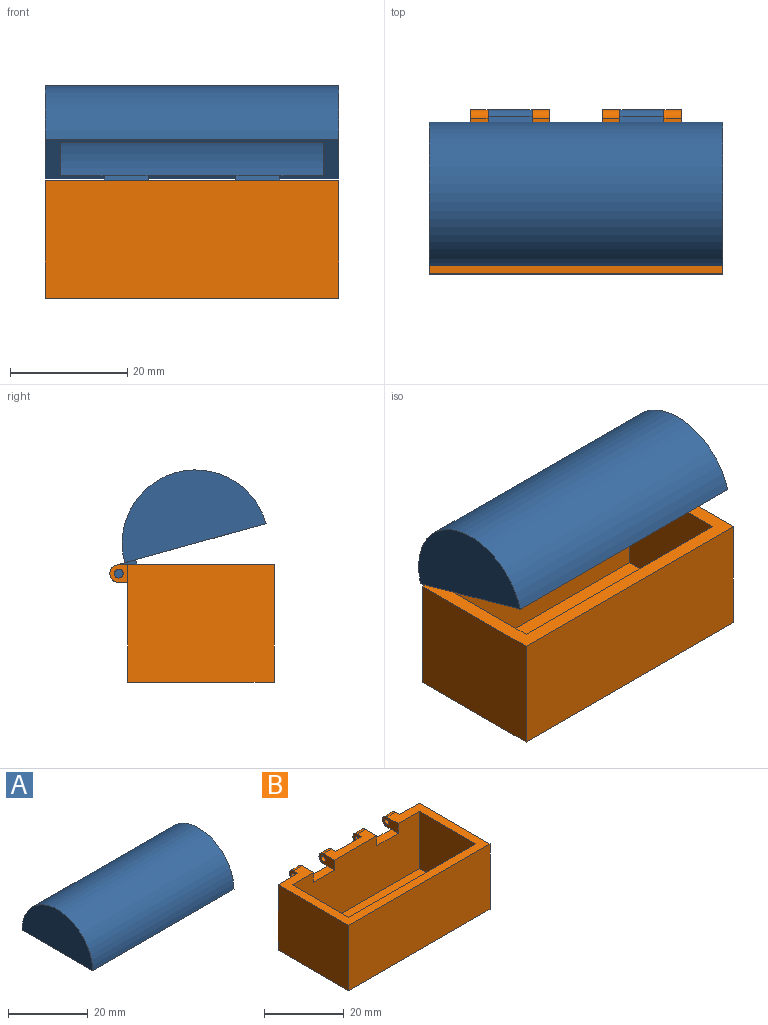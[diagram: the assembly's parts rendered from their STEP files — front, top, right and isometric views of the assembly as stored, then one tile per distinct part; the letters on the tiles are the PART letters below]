
ASSEMBLY  parts=2 mates=1
PART A: 28 faces, bbox 50x28x15.5 mm
  f0: plane 4.92x3mm, normal (-1,0,0), area 12mm2, adj f2,f7,f9,f16,f19,f22
  f1: plane 4.92x3mm, normal (1,0,0), area 12mm2, adj f2,f7,f8,f16,f19,f20
  f2: plane 7.5x3.42mm, normal (0,0,-1), area 25.7mm2, adj f0,f1,f16,f19
  f3: plane 4.92x3mm, normal (1,0,0), area 12mm2, adj f5,f6,f9,f17,f18,f26
  f4: plane 4.92x3mm, normal (-1,0,0), area 12mm2, adj f5,f6,f8,f17,f18,f24
  f5: plane 7.5x3.42mm, normal (0,0,-1), area 25.7mm2, adj f3,f4,f17,f18
  f6: plane 7.5x1.5mm, normal (0,0,1), area 11.2mm2, adj f3,f4,f10,f18
  f7: plane 7.5x1.5mm, normal (0,0,1), area 11.2mm2, adj f0,f1,f10,f19
  f8: plane 50x25mm, normal (0,0,-1), area 240.4mm2, adj f1,f4,f10,f11,f12,f13,f14,f15
  f9: plane 15x1.92mm, normal (0,0,-1), area 28.9mm2, adj f0,f3,f10,f13
  f10: cylinder r=12.5mm len=50mm, axis (1,0,0), area 1963.5mm2, adj f6,f7,f8,f9,f11,f12
  f11: plane 25x12.5mm, normal (-1,0,0), area 245.4mm2, adj f8,f10
  f12: plane 25x12.5mm, normal (1,0,0), area 245.4mm2, adj f8,f10
  f13: cylinder r=10.58mm len=45mm, axis (1,0,0), area 1495.1mm2, adj f8,f9,f14,f15,f16,f17
  f14: plane 21.15x10.58mm, normal (1,0,0), area 175.7mm2, adj f8,f13
  f15: plane 21.15x10.58mm, normal (-1,0,0), area 175.7mm2, adj f8,f13
  f16: plane 7.5x3mm, normal (0,-1,0), area 22.5mm2, adj f0,f1,f2,f13
  f17: plane 7.5x3mm, normal (0,-1,0), area 22.5mm2, adj f3,f4,f5,f13
  f18: cylinder r=1.5mm len=7.5mm, axis (1,0,0), area 35.3mm2, adj f3,f4,f5,f6
  f19: cylinder r=1.5mm len=7.5mm, axis (1,0,0), area 35.3mm2, adj f0,f1,f2,f7
  f20: cylinder r=0.75mm len=3mm, axis (-1,0,0), area 14.1mm2, adj f1,f21
  f21: plane 1.5x1.5mm, normal (1,0,0), area 1.8mm2, adj f20
  f22: cylinder r=0.75mm len=3mm, axis (1,0,0), area 14.1mm2, adj f0,f23
  f23: plane 1.5x1.5mm, normal (-1,0,0), area 1.8mm2, adj f22
  f24: cylinder r=0.75mm len=3mm, axis (1,0,0), area 14.1mm2, adj f4,f25
  f25: plane 1.5x1.5mm, normal (-1,0,0), area 1.8mm2, adj f24
  f26: cylinder r=0.75mm len=3mm, axis (-1,0,0), area 14.1mm2, adj f3,f27
  f27: plane 1.5x1.5mm, normal (1,0,0), area 1.8mm2, adj f26
PART B: 243 faces, bbox 50x28x20 mm
  f0: plane 50x25mm, normal (0,0,-1), area 1214.1mm2, adj f12,f13,f14,f15,f34,f35,f36,f37
  f1: plane 5.5x3mm, normal (1,0,0), area 13.8mm2, adj f5,f17,f22,f25,f30,f31
  f2: plane 5.5x3mm, normal (-1,0,0), area 13.8mm2, adj f4,f17,f22,f23,f32,f33
  f3: plane 3x3mm, normal (-1,0,0), area 6.3mm2, adj f5,f12,f25,f30,f31
  f4: plane 50x26.5mm, normal (0,0,1), area 284mm2, adj f2,f7,f10,f12,f13,f14,f15,f16
  f5: plane 15x4mm, normal (0,0,1), area 46.5mm2, adj f1,f3,f6,f8,f12,f17,f28,f31
  f6: plane 5.5x3mm, normal (-1,0,0), area 13.8mm2, adj f5,f9,f17,f21,f27,f28
  f7: plane 5.5x3mm, normal (1,0,0), area 13.8mm2, adj f4,f11,f17,f21,f26,f29
  f8: plane 3x3mm, normal (1,0,0), area 6.3mm2, adj f5,f9,f12,f27,f28
  f9: plane 3x1.5mm, normal (0,0,-1), area 4.5mm2, adj f6,f8,f12,f28
  f10: plane 3x3mm, normal (-1,0,0), area 6.3mm2, adj f4,f11,f12,f26,f29
  f11: plane 3x1.5mm, normal (0,0,-1), area 4.5mm2, adj f7,f10,f12,f29
  f12: plane 50x20mm, normal (0,1,0), area 919mm2, adj f0,f3,f4,f5,f8,f9,f10,f11
  f13: plane 25x20mm, normal (1,0,0), area 500mm2, adj f0,f4,f12,f15
  f14: plane 25x20mm, normal (-1,0,0), area 500mm2, adj f0,f4,f12,f15
  f15: plane 50x20mm, normal (0,-1,0), area 1000mm2, adj f0,f4,f13,f14
  f16: plane 20x17.5mm, normal (-1,0,0), area 350mm2, adj f4,f17,f19,f20
  f17: plane 45x17.5mm, normal (0,-1,0), area 742.5mm2, adj f1,f2,f4,f5,f6,f7,f16,f18
  f18: plane 20x17.5mm, normal (1,0,0), area 350mm2, adj f4,f17,f19,f20
  f19: plane 45x17.5mm, normal (0,1,0), area 787.5mm2, adj f4,f16,f18,f20
  f20: plane 45x20mm, normal (0,0,1), area 900mm2, adj f16,f17,f18,f19
  f21: plane 7.5x2.5mm, normal (0,0,1), area 18.8mm2, adj f6,f7,f12,f17
  f22: plane 7.5x2.5mm, normal (0,0,1), area 18.8mm2, adj f1,f2,f12,f17
  f23: plane 3x1.5mm, normal (0,0,-1), area 4.5mm2, adj f2,f12,f24,f33
  f24: plane 3x3mm, normal (1,0,0), area 6.3mm2, adj f4,f12,f23,f32,f33
  f25: plane 3x1.5mm, normal (0,0,-1), area 4.5mm2, adj f1,f3,f12,f31
  f26: cylinder r=0.75mm len=3mm, axis (-1,0,0), area 14.1mm2, adj f7,f10
  f27: cylinder r=0.75mm len=3mm, axis (-1,0,0), area 14.1mm2, adj f6,f8
  f28: cylinder r=1.5mm len=3mm, axis (-1,0,0), area 14.1mm2, adj f5,f6,f8,f9
  f29: cylinder r=1.5mm len=3mm, axis (-1,0,0), area 14.1mm2, adj f4,f7,f10,f11
  f30: cylinder r=0.75mm len=3mm, axis (1,0,0), area 14.1mm2, adj f1,f3
  f31: cylinder r=1.5mm len=3mm, axis (1,0,0), area 14.1mm2, adj f1,f3,f5,f25
  f32: cylinder r=0.75mm len=3mm, axis (1,0,0), area 14.1mm2, adj f2,f24
  f33: cylinder r=1.5mm len=3mm, axis (1,0,0), area 14.1mm2, adj f2,f4,f23,f24
  f34: plane 1x0.27mm, normal (-0.53,-0.85,0), area 0.3mm2, adj f0,f35,f37,f38
  f35: extruded ~1x0.63mm, area 0.7mm2, adj f0,f34,f36,f38
  f36: plane 1x0.26mm, normal (0.49,0.87,0), area 0.3mm2, adj f0,f35,f37,f38
  f37: extruded ~1x0.65mm, area 0.7mm2, adj f0,f34,f36,f38
  f38: plane 0.8x0.61mm, normal (0,0,-1), area 0.2mm2, adj f34,f35,f36,f37
  f39: plane 1x0.95mm, normal (-1,0,0), area 1mm2, adj f40,f58,f59,f240
  f40: plane 1.26x1mm, normal (0,-1,0), area 1.3mm2, adj f39,f41,f59,f240
  f41: plane 1x0.95mm, normal (1,0,0), area 1mm2, adj f40,f58,f59,f240
  f42: plane 1.26x1mm, normal (0,-1,0), area 1.3mm2, adj f43,f55,f59,f61
  f43: plane 1x0.91mm, normal (1,0,0), area 0.9mm2, adj f42,f44,f59,f61
  f44: plane 1.26x1mm, normal (0,1,0), area 1.3mm2, adj f43,f55,f59,f61
  f45: plane 1x0.93mm, normal (1,0,0), area 0.9mm2, adj f46,f56,f59,f60
  f46: plane 1.26x1mm, normal (0,1,0), area 1.3mm2, adj f45,f47,f59,f60
  f47: plane 1x0.93mm, normal (-1,0,0), area 0.9mm2, adj f46,f56,f59,f60
  f48: plane 1x0.33mm, normal (0,1,0), area 0.3mm2, adj f0,f49,f57,f59
  f49: plane 3.78x1mm, normal (-1,0,0), area 3.8mm2, adj f0,f48,f50,f59
  f50: plane 1.94x1mm, normal (0,1,0), area 1.9mm2, adj f0,f49,f51,f59
  f51: plane 3.78x1mm, normal (1,0,0), area 3.8mm2, adj f0,f50,f52,f59
  f52: plane 1x0.43mm, normal (0,1,0), area 0.4mm2, adj f0,f51,f53,f59
  f53: plane 1x0.33mm, normal (1,0,0), area 0.3mm2, adj f0,f52,f54,f59
  f54: plane 2.7x1mm, normal (0,-1,0), area 2.7mm2, adj f0,f53,f57,f59
  f55: plane 1x0.91mm, normal (-1,0,0), area 0.9mm2, adj f42,f44,f59,f61
  f56: plane 1.26x1mm, normal (0,-1,0), area 1.3mm2, adj f45,f47,f59,f60
  f57: plane 1x0.33mm, normal (-1,0,0), area 0.3mm2, adj f0,f48,f54,f59
  f58: plane 1.26x1mm, normal (0,1,0), area 1.3mm2, adj f39,f41,f59,f240
  f59: plane 4.11x2.7mm, normal (0,0,-1), area 4.7mm2, adj f39,f40,f41,f42,f43,f44,f45,f46
  f60: plane 1.26x0.93mm, normal (0,0,-1), area 1.2mm2, adj f45,f46,f47,f56
  f61: plane 1.26x0.91mm, normal (0,0,-1), area 1.1mm2, adj f42,f43,f44,f55
  f62: plane 2.12x1mm, normal (0,1,0), area 2.1mm2, adj f0,f63,f81,f82
  f63: plane 1x0.35mm, normal (1,0,0), area 0.3mm2, adj f0,f62,f64,f82
  f64: plane 1x0.61mm, normal (0,-1,0), area 0.6mm2, adj f0,f63,f65,f82
  f65: plane 1.44x1mm, normal (1,0,0), area 1.4mm2, adj f0,f64,f66,f82
  f66: plane 1x0.66mm, normal (0,1,0), area 0.7mm2, adj f0,f65,f67,f82
  f67: plane 1x0.34mm, normal (1,0,0), area 0.3mm2, adj f0,f66,f68,f82
  f68: plane 1x0.66mm, normal (0,-1,0), area 0.7mm2, adj f0,f67,f69,f82
  f69: plane 2.06x1mm, normal (1,0,0), area 2.1mm2, adj f0,f68,f70,f82
  f70: plane 1x0.34mm, normal (0,-1,0), area 0.3mm2, adj f0,f69,f71,f82
  f71: plane 2.06x1mm, normal (-1,0,0), area 2.1mm2, adj f0,f70,f72,f82
  f72: plane 1x0.64mm, normal (0,-1,0), area 0.6mm2, adj f0,f71,f73,f82
  f73: plane 1x0.34mm, normal (-1,0,0), area 0.3mm2, adj f0,f72,f74,f82
  f74: plane 1x0.64mm, normal (0,1,0), area 0.6mm2, adj f0,f73,f75,f82
  f75: plane 1.44x1mm, normal (-1,0,0), area 1.4mm2, adj f0,f74,f76,f82
  f76: plane 1x0.81mm, normal (0,-1,0), area 0.8mm2, adj f0,f75,f77,f82
  f77: extruded ~3.74x1mm, area 3.9mm2, adj f0,f76,f78,f82
  f78: extruded ~1x0.77mm, area 1mm2, adj f0,f77,f79,f82
  f79: extruded ~1x0.26mm, area 0.3mm2, adj f0,f78,f80,f82
  f80: extruded ~1x0.65mm, area 0.7mm2, adj f0,f79,f81,f82
  f81: extruded ~3.73x1mm, area 3.8mm2, adj f0,f62,f80,f82
  f82: plane 4.18x2.7mm, normal (0,0,-1), area 4mm2, adj f62,f63,f64,f65,f66,f67,f68,f69
  f83: plane 1x0.29mm, normal (1,0,0), area 0.3mm2, adj f0,f84,f86,f87
  f84: plane 1.38x1mm, normal (0,-1,0), area 1.4mm2, adj f0,f83,f85,f87
  f85: plane 1x0.29mm, normal (-1,0,0), area 0.3mm2, adj f0,f84,f86,f87
  f86: plane 1.38x1mm, normal (0,1,0), area 1.4mm2, adj f0,f83,f85,f87
  f87: plane 1.38x0.29mm, normal (0,0,-1), area 0.4mm2, adj f83,f84,f85,f86
  f88: plane 1.37x1mm, normal (0,-1,0), area 1.4mm2, adj f0,f89,f91,f92
  f89: plane 1x0.29mm, normal (-1,0,0), area 0.3mm2, adj f0,f88,f90,f92
  f90: plane 1.37x1mm, normal (0,1,0), area 1.4mm2, adj f0,f89,f91,f92
  f91: plane 1x0.29mm, normal (1,0,0), area 0.3mm2, adj f0,f88,f90,f92
  f92: plane 1.37x0.29mm, normal (0,0,-1), area 0.4mm2, adj f88,f89,f90,f91
  f93: plane 1x0.3mm, normal (-1,0,0), area 0.3mm2, adj f0,f94,f96,f97
  f94: plane 1.75x1mm, normal (0,1,0), area 1.8mm2, adj f0,f93,f95,f97
  f95: plane 1x0.3mm, normal (1,0,0), area 0.3mm2, adj f0,f94,f96,f97
  f96: plane 1.75x1mm, normal (0,-1,0), area 1.8mm2, adj f0,f93,f95,f97
  f97: plane 1.75x0.3mm, normal (0,0,-1), area 0.5mm2, adj f93,f94,f95,f96
  f98: plane 3.48x1mm, normal (0,1,0), area 3.5mm2, adj f0,f99,f101,f102
  f99: plane 1x0.39mm, normal (1,0,0), area 0.4mm2, adj f0,f98,f100,f102
  f100: plane 3.48x1mm, normal (0,-1,0), area 3.5mm2, adj f0,f99,f101,f102
  f101: plane 1x0.39mm, normal (-1,0,0), area 0.4mm2, adj f0,f98,f100,f102
  f102: plane 3.48x0.39mm, normal (0,0,-1), area 1.3mm2, adj f98,f99,f100,f101
  f103: plane 4.3x1mm, normal (0,1,0), area 4.3mm2, adj f0,f104,f106,f107
  f104: plane 1x0.4mm, normal (1,0,0), area 0.4mm2, adj f0,f103,f105,f107
  f105: plane 4.3x1mm, normal (0,-1,0), area 4.3mm2, adj f0,f104,f106,f107
  f106: plane 1x0.4mm, normal (-1,0,0), area 0.4mm2, adj f0,f103,f105,f107
  f107: plane 4.3x0.4mm, normal (0,0,-1), area 1.7mm2, adj f103,f104,f105,f106
  f108: plane 1x0.26mm, normal (1,0,0), area 0.3mm2, adj f0,f109,f119,f120
  f109: plane 2.25x1mm, normal (0,-1,0), area 2.3mm2, adj f0,f108,f110,f120
  f110: plane 1x0.39mm, normal (-1,0,0), area 0.4mm2, adj f0,f109,f111,f120
  f111: plane 1x0.99mm, normal (0,1,0), area 1mm2, adj f0,f110,f112,f120
  f112: extruded ~1x0.59mm, area 0.6mm2, adj f0,f111,f113,f120
  f113: extruded ~2.24x1.4mm, area 2.7mm2, adj f0,f112,f114,f120
  f114: extruded ~1.06x1.04mm, area 1.7mm2, adj f0,f113,f115,f120
  f115: extruded ~1.05x1mm, area 1.2mm2, adj f0,f114,f116,f120
  f116: plane 1x0.26mm, normal (0.7,-0.71,0), area 0.4mm2, adj f0,f115,f117,f120
  f117: extruded ~1x0.74mm, area 0.9mm2, adj f0,f116,f118,f120
  f118: extruded ~1x0.71mm, area 1.1mm2, adj f0,f117,f119,f120
  f119: extruded ~2.31x1.64mm, area 2.9mm2, adj f0,f108,f118,f120
  f120: plane 3.65x2.27mm, normal (0,0,-1), area 2.9mm2, adj f108,f109,f110,f111,f112,f113,f114,f115
  f121: plane 1x0.42mm, normal (0,-1,0), area 0.4mm2, adj f0,f122,f133,f134
  f122: plane 1x0.19mm, normal (0.61,0.8,0), area 0.2mm2, adj f0,f121,f123,f134
  f123: extruded ~1x0.5mm, area 0.7mm2, adj f0,f122,f124,f134
  f124: plane 1x0.24mm, normal (-0.64,-0.77,0), area 0.3mm2, adj f0,f123,f125,f134
  f125: extruded ~1x0.44mm, area 0.6mm2, adj f0,f124,f126,f134
  f126: plane 1x0.92mm, normal (0,-1,0), area 0.9mm2, adj f0,f125,f127,f134
  f127: plane 1x0.29mm, normal (-1,0,0), area 0.3mm2, adj f0,f126,f128,f134
  f128: plane 1.25x1mm, normal (0,1,0), area 1.3mm2, adj f0,f127,f129,f134
  f129: extruded ~1x0.29mm, area 0.3mm2, adj f0,f128,f130,f134
  f130: plane 1x0.32mm, normal (-0.27,0.96,0), area 0.3mm2, adj f0,f129,f131,f134
  f131: extruded ~1.06x1mm, area 1.3mm2, adj f0,f130,f132,f134
  f132: extruded ~1x0.25mm, area 0.3mm2, adj f0,f131,f133,f134
  f133: extruded ~1x0.63mm, area 0.8mm2, adj f0,f121,f132,f134
  f134: plane 2.17x1.31mm, normal (0,0,-1), area 1mm2, adj f121,f122,f123,f124,f125,f126,f127,f128
  f135: plane 1.1x1mm, normal (0,-1,0), area 1.1mm2, adj f136,f168,f169,f241
  f136: plane 1x0.45mm, normal (1,0,0), area 0.5mm2, adj f135,f137,f169,f241
  f137: plane 1.17x1mm, normal (0,1,0), area 1.2mm2, adj f136,f168,f169,f241
  f138: plane 1x0.45mm, normal (-1,0,0), area 0.4mm2, adj f139,f166,f169,f170
  f139: plane 1.28x1mm, normal (0,-1,0), area 1.3mm2, adj f138,f140,f169,f170
  f140: plane 1x0.45mm, normal (1,0,0), area 0.4mm2, adj f139,f166,f169,f170
  f141: plane 1.8x1mm, normal (0,1,0), area 1.8mm2, adj f0,f142,f167,f169
  f142: plane 1x0.45mm, normal (-1,0,0), area 0.5mm2, adj f0,f141,f143,f169
  f143: plane 1.64x1mm, normal (0,-1,0), area 1.6mm2, adj f0,f142,f144,f169
  f144: plane 1.06x1mm, normal (-1,0,0), area 1.1mm2, adj f0,f143,f145,f169
  f145: plane 3.57x1mm, normal (0,1,0), area 3.6mm2, adj f0,f144,f146,f169
  f146: plane 1x0.31mm, normal (1,0,0), area 0.3mm2, adj f0,f145,f147,f169
  f147: plane 1.58x1mm, normal (0,-1,0), area 1.6mm2, adj f0,f146,f148,f169
  f148: plane 1x0.45mm, normal (1,0,0), area 0.4mm2, adj f0,f147,f149,f169
  f149: plane 1.41x1mm, normal (0,1,0), area 1.4mm2, adj f0,f148,f150,f169
  f150: extruded ~1.07x1mm, area 1.1mm2, adj f0,f149,f151,f169
  f151: plane 1.29x1mm, normal (0,-1,0), area 1.3mm2, adj f0,f150,f152,f169
  f152: extruded ~1.59x1mm, area 1.9mm2, adj f0,f151,f153,f169
  f153: extruded ~1x0.29mm, area 0.4mm2, adj f0,f152,f154,f169
  f154: extruded ~1.64x1.13mm, area 2mm2, adj f0,f153,f155,f169
  f155: plane 1.12x1mm, normal (1,0,0), area 1.1mm2, adj f0,f154,f156,f169
  f156: plane 1x0.36mm, normal (0,-1,0), area 0.4mm2, adj f0,f155,f157,f169
  f157: plane 1.26x1mm, normal (-1,0,0), area 1.3mm2, adj f0,f156,f158,f169
  f158: plane 1.41x1mm, normal (0,-1,0), area 1.4mm2, adj f0,f157,f159,f169
  f159: extruded ~1x0.7mm, area 0.7mm2, adj f0,f158,f160,f169
  f160: extruded ~1x0.18mm, area 0.2mm2, adj f0,f159,f161,f169
  f161: extruded ~1x0.55mm, area 0.6mm2, adj f0,f160,f162,f169
  f162: extruded ~1x0.34mm, area 0.4mm2, adj f0,f161,f163,f169
  f163: extruded ~1x0.62mm, area 0.6mm2, adj f0,f162,f164,f169
  f164: extruded ~1x0.3mm, area 0.3mm2, adj f0,f163,f165,f169
  f165: extruded ~1.09x1mm, area 1.1mm2, adj f0,f164,f167,f169
  f166: plane 1.28x1mm, normal (0,1,0), area 1.3mm2, adj f138,f140,f169,f170
  f167: extruded ~1x0.15mm, area 0.2mm2, adj f0,f141,f165,f169
  f168: extruded ~1x0.45mm, area 0.5mm2, adj f135,f137,f169,f241
  f169: plane 4.03x3.09mm, normal (0,0,-1), area 5.6mm2, adj f135,f136,f137,f138,f139,f140,f141,f142
  f170: plane 1.28x0.45mm, normal (0,0,-1), area 0.6mm2, adj f138,f139,f140,f166
  f171: plane 1x0.79mm, normal (0,-1,0), area 0.8mm2, adj f172,f180,f181,f242
  f172: plane 1x0.81mm, normal (1,0,0), area 0.8mm2, adj f171,f173,f181,f242
  f173: plane 1x0.79mm, normal (0,1,0), area 0.8mm2, adj f172,f180,f181,f242
  f174: plane 1.41x1mm, normal (-1,0,0), area 1.4mm2, adj f0,f175,f179,f181
  f175: plane 1.38x1mm, normal (0,1,0), area 1.4mm2, adj f0,f174,f176,f181
  f176: plane 1.64x1mm, normal (1,0,0), area 1.6mm2, adj f0,f175,f177,f181
  f177: plane 1x0.29mm, normal (0,-1,0), area 0.3mm2, adj f0,f176,f178,f181
  f178: plane 1x0.23mm, normal (-1,0,0), area 0.2mm2, adj f0,f177,f179,f181
  f179: plane 1.09x1mm, normal (0,-1,0), area 1.1mm2, adj f0,f174,f178,f181
  f180: plane 1x0.81mm, normal (-1,0,0), area 0.8mm2, adj f171,f173,f181,f242
  f181: plane 1.64x1.38mm, normal (0,0,-1), area 1.4mm2, adj f171,f172,f173,f174,f175,f176,f177,f178
  f182: plane 1x0.27mm, normal (0.31,0.95,0), area 0.3mm2, adj f0,f183,f185,f186
  f183: extruded ~1x0.84mm, area 0.9mm2, adj f0,f182,f184,f186
  f184: plane 1x0.29mm, normal (-0.32,-0.95,0), area 0.3mm2, adj f0,f183,f185,f186
  f185: extruded ~1x0.83mm, area 0.9mm2, adj f0,f182,f184,f186
  f186: plane 0.93x0.53mm, normal (0,0,-1), area 0.3mm2, adj f182,f183,f184,f185
  f187: plane 1x0.29mm, normal (0.18,0.98,0), area 0.3mm2, adj f0,f188,f190,f191
  f188: extruded ~1.05x1mm, area 1.1mm2, adj f0,f187,f189,f191
  f189: plane 1x0.31mm, normal (-0.19,-0.98,0), area 0.3mm2, adj f0,f188,f190,f191
  f190: extruded ~1.05x1mm, area 1.1mm2, adj f0,f187,f189,f191
  f191: plane 1.1x0.43mm, normal (0,0,-1), area 0.3mm2, adj f187,f188,f189,f190
  f192: plane 1x0.31mm, normal (-0.16,0.99,0), area 0.3mm2, adj f0,f193,f195,f196
  f193: extruded ~1.12x1mm, area 1.1mm2, adj f0,f192,f194,f196
  f194: extruded ~1x0.3mm, area 0.3mm2, adj f0,f193,f195,f196
  f195: extruded ~1.18x1mm, area 1.2mm2, adj f0,f192,f194,f196
  f196: plane 1.23x0.54mm, normal (0,0,-1), area 0.4mm2, adj f192,f193,f194,f195
  f197: plane 1x0.3mm, normal (-0.31,-0.95,0), area 0.3mm2, adj f0,f198,f216,f217
  f198: extruded ~1.01x1mm, area 1.1mm2, adj f0,f197,f199,f217
  f199: plane 1x0.28mm, normal (0.28,0.96,0), area 0.3mm2, adj f0,f198,f200,f217
  f200: extruded ~1x0.45mm, area 0.5mm2, adj f0,f199,f201,f217
  f201: plane 1x0.86mm, normal (0.13,0.99,0), area 0.9mm2, adj f0,f200,f202,f217
  f202: extruded ~1.56x1.16mm, area 1.9mm2, adj f0,f201,f203,f217
  f203: plane 1x0.31mm, normal (-0.52,0.85,0), area 0.4mm2, adj f0,f202,f204,f217
  f204: extruded ~1x0.64mm, area 0.7mm2, adj f0,f203,f205,f217
  f205: plane 1x0.57mm, normal (0.09,1,0), area 0.6mm2, adj f0,f204,f206,f217
  f206: extruded ~1.3x1mm, area 1.5mm2, adj f0,f205,f207,f217
  f207: plane 1x0.33mm, normal (-0.39,0.92,0), area 0.4mm2, adj f0,f206,f208,f217
  f208: extruded ~1.24x1mm, area 1.4mm2, adj f0,f207,f209,f217
  f209: extruded ~1x0.28mm, area 0.4mm2, adj f0,f208,f210,f217
  f210: extruded ~1x0.33mm, area 0.3mm2, adj f0,f209,f211,f217
  f211: extruded ~1x0.74mm, area 0.7mm2, adj f0,f210,f212,f217
  f212: extruded ~1x0.56mm, area 0.7mm2, adj f0,f211,f213,f217
  f213: extruded ~1x0.37mm, area 0.5mm2, adj f0,f212,f214,f217
  f214: extruded ~1x0.34mm, area 0.4mm2, adj f0,f213,f215,f217
  f215: extruded ~1.41x1mm, area 1.4mm2, adj f0,f214,f216,f217
  f216: extruded ~1x0.29mm, area 0.3mm2, adj f0,f197,f215,f217
  f217: plane 2.96x1.92mm, normal (0,0,-1), area 2.3mm2, adj f197,f198,f199,f200,f201,f202,f203,f204
  f218: extruded ~3.2x1.01mm, area 3.4mm2, adj f0,f219,f224,f225
  f219: plane 1x0.46mm, normal (0,-1,0), area 0.5mm2, adj f0,f218,f220,f225
  f220: extruded ~3.31x1.05mm, area 3.5mm2, adj f0,f219,f221,f225
  f221: plane 1x0.27mm, normal (-1,0,0), area 0.3mm2, adj f0,f220,f222,f225
  f222: plane 2.24x1mm, normal (0,1,0), area 2.2mm2, adj f0,f221,f223,f225
  f223: plane 1x0.38mm, normal (1,0,0), area 0.4mm2, adj f0,f222,f224,f225
  f224: plane 1.73x1mm, normal (0,-1,0), area 1.7mm2, adj f0,f218,f223,f225
  f225: plane 3.58x2.24mm, normal (0,0,-1), area 2.2mm2, adj f218,f219,f220,f221,f222,f223,f224
  f226: plane 1.47x1mm, normal (0,1,0), area 1.5mm2, adj f0,f227,f238,f239
  f227: extruded ~1x0.31mm, area 0.3mm2, adj f0,f226,f228,f239
  f228: plane 1x0.34mm, normal (-0.23,0.97,0), area 0.3mm2, adj f0,f227,f229,f239
  f229: extruded ~1x0.91mm, area 1.1mm2, adj f0,f228,f230,f239
  f230: extruded ~1x0.27mm, area 0.3mm2, adj f0,f229,f231,f239
  f231: extruded ~1x0.45mm, area 0.6mm2, adj f0,f230,f232,f239
  f232: plane 1x0.55mm, normal (0,-1,0), area 0.5mm2, adj f0,f231,f233,f239
  f233: plane 1x0.21mm, normal (0.63,0.78,0), area 0.3mm2, adj f0,f232,f234,f239
  f234: extruded ~1x0.5mm, area 0.7mm2, adj f0,f233,f235,f239
  f235: plane 1x0.24mm, normal (-0.65,-0.76,0), area 0.3mm2, adj f0,f234,f236,f239
  f236: extruded ~1x0.48mm, area 0.7mm2, adj f0,f235,f237,f239
  f237: plane 1.05x1mm, normal (0,-1,0), area 1mm2, adj f0,f236,f238,f239
  f238: plane 1x0.29mm, normal (-1,0,0), area 0.3mm2, adj f0,f226,f237,f239
  f239: plane 2.29x1.32mm, normal (0,0,-1), area 1.1mm2, adj f226,f227,f228,f229,f230,f231,f232,f233
  f240: plane 1.26x0.95mm, normal (0,0,-1), area 1.2mm2, adj f39,f40,f41,f58
  f241: plane 1.17x0.45mm, normal (0,0,-1), area 0.5mm2, adj f135,f136,f137,f168
  f242: plane 0.81x0.79mm, normal (0,0,-1), area 0.6mm2, adj f171,f172,f173,f180
PLACE A rot(axis=(-1,0,0),15.5deg) t=(28.38,3.62,14.53)mm
PLACE B t=(3.38,2.71,-9.17)mm fixed
MATE revolute A.f18 <-> B.f26  axis (1,0,0) through (21.38,16.71,9.33)mm
